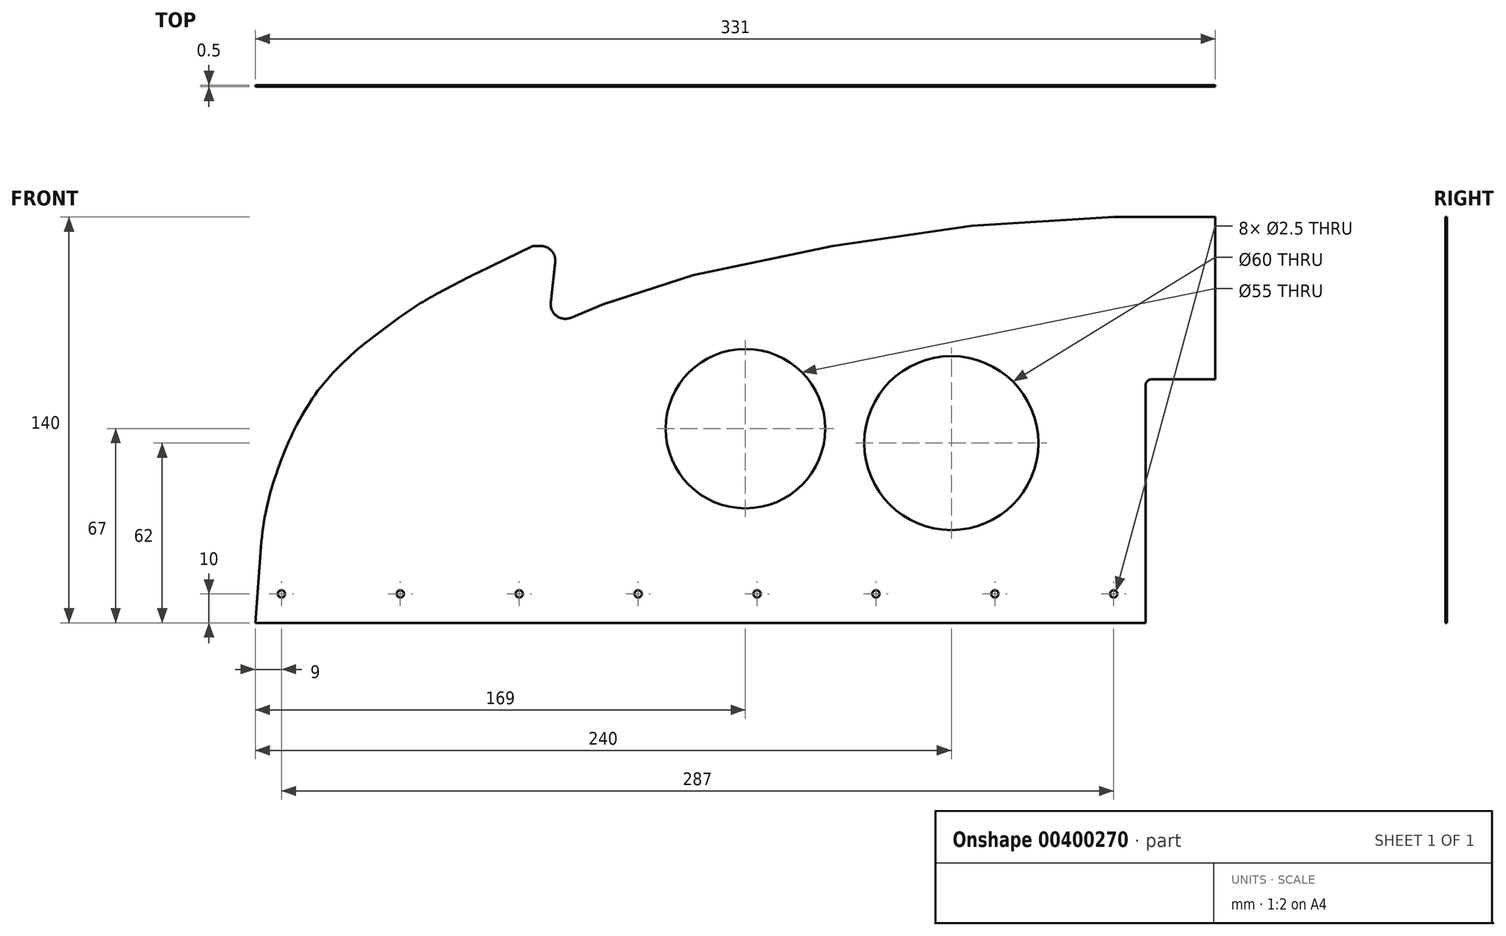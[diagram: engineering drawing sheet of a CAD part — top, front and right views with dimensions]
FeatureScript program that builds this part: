
annotation { "Feature Type Name" : "Feature", "Feature Type Description" : "" }
export const myFeature = defineFeature(function(context is Context, id is Id, definition is map)
    precondition{}
    {
        {
            var Q0;
            Q0=qCreatedBy(makeId("Front.planeOp"),FACE);
            var sketch = newSketch(context, id + "F0", { "sketchPlane" : qUnion([Q0])});
            skLineSegment(sketch, "E0", {"start": v(-24, 0) * mm, "end": v(-331, 0) * mm});
            skLineSegment(sketch, "E1", {"start": v(0, 84) * mm, "end": v(0, 140) * mm});
            skLineSegment(sketch, "E2", {"start": v(-331, 0) * mm, "end": v(-328, 40) * mm});
            skLineSegment(sketch, "E3", {"start": v(-328, 40) * mm, "end": v(-317, 70) * mm});
            skLineSegment(sketch, "E4", {"start": v(-317, 70) * mm, "end": v(-302, 90) * mm});
            skLineSegment(sketch, "E5", {"start": v(-302, 90) * mm, "end": v(-275, 110) * mm});
            skLineSegment(sketch, "E6", {"start": v(-275, 110) * mm, "end": v(-256, 120) * mm});
            skLineSegment(sketch, "E7", {"start": v(-256, 120) * mm, "end": v(-235.28, 130) * mm});
            skLineSegment(sketch, "E8", {"start": v(-235.28, 130) * mm, "end": v(-227, 130) * mm});
            skLineSegment(sketch, "E9", {"start": v(-227, 130) * mm, "end": v(-230, 102) * mm});
            skLineSegment(sketch, "E10", {"start": v(-132, 130) * mm, "end": v(-84, 137) * mm});
            skLineSegment(sketch, "E11", {"start": v(-84, 137) * mm, "end": v(-35, 140) * mm});
            skLineSegment(sketch, "E12", {"start": v(-35, 140) * mm, "end": v(0, 140) * mm});
            skLineSegment(sketch, "E13", {"start": v(-24, 0) * mm, "end": v(-24, 84) * mm});
            skLineSegment(sketch, "E14", {"start": v(-24, 84) * mm, "end": v(0, 84) * mm});
            skLineSegment(sketch, "E15", {"start": v(-132, 130) * mm, "end": v(-180, 120) * mm});
            skLineSegment(sketch, "E16", {"start": v(-180, 120) * mm, "end": v(-211, 110) * mm});
            skLineSegment(sketch, "E17", {"start": v(-211, 110) * mm, "end": v(-230, 102) * mm});
            skCircle(sketch, "E18", {"center": v(-91, 62) * mm, "radius": 30 * mm});
            skCircle(sketch, "E19", {"center": v(-162, 67) * mm, "radius": 27.5 * mm});
            skCircle(sketch, "E20", {"center": v(-35, 10) * mm, "radius": 1.25 * mm});
            skCircle(sketch, "E21.1.0.0", {"center": v(-76, 10) * mm, "radius": 1.25 * mm});
            skLineSegment(sketch, "E21.1.0.1", {"start": v(-65, 0) * mm, "end": v(-65, 84) * mm});
            skCircle(sketch, "E21.2.0.0", {"center": v(-117, 10) * mm, "radius": 1.25 * mm});
            skLineSegment(sketch, "E21.2.0.1", {"start": v(-106, 0) * mm, "end": v(-106, 84) * mm});
            skCircle(sketch, "E21.3.0.0", {"center": v(-158, 10) * mm, "radius": 1.25 * mm});
            skLineSegment(sketch, "E21.3.0.1", {"start": v(-147, 0) * mm, "end": v(-147, 84) * mm});
            skCircle(sketch, "E21.4.0.0", {"center": v(-199, 10) * mm, "radius": 1.25 * mm});
            skLineSegment(sketch, "E21.4.0.1", {"start": v(-188, 0) * mm, "end": v(-188, 84) * mm});
            skLineSegment(sketch, "E21.direction1", {"start": v(-35, 10) * mm, "end": v(-76, 10) * mm, "construction": true});
            skCircle(sketch, "E22.0.5.0", {"center": v(-240, 10) * mm, "radius": 1.25 * mm});
            skLineSegment(sketch, "E22.2.5.0", {"start": v(-229, 0) * mm, "end": v(-229, 84) * mm});
            skCircle(sketch, "E22.0.6.0", {"center": v(-281, 10) * mm, "radius": 1.25 * mm});
            skLineSegment(sketch, "E22.2.6.0", {"start": v(-270, 0) * mm, "end": v(-270, 84) * mm});
            skCircle(sketch, "E22.0.7.0", {"center": v(-322, 10) * mm, "radius": 1.25 * mm});
            skLineSegment(sketch, "E22.2.7.0", {"start": v(-311, 0) * mm, "end": v(-311, 84) * mm});
            skSolve(sketch);
        }
        {
            var Q0;
            Q0=makeQuery(id+"F0.imprint","IMPRINT",FACE,{"disambiguationData":[TD([[makeQuery(id+"F0.imprint","IMPRINT",EDGE,{"derivedFrom":sQuery(id+"F0.wireOp",EDGE,"E1")}),1.0]])]});
            var Q1;
            {var subQ1=sQuery(id+"F0.wireOp",EDGE,"E2");Q1=makeQuery(id+"F0.imprint","IMPRINT",FACE,{"disambiguationData":[TD([[makeQuery(id+"F0.imprint","IMPRINT",EDGE,{"derivedFrom":subQ1}),-1.0]])]});}
            var Q2;
            Q2=makeQuery(id+"F0.imprint","IMPRINT",FACE,{"disambiguationData":[TD([[makeQuery(id+"F0.imprint","IMPRINT",EDGE,{"derivedFrom":sQuery(id+"F0.wireOp",EDGE,"E21.3.0.0")}),-1.0]])]});
            var Q3;
            Q3=makeQuery(id+"F0.imprint","IMPRINT",FACE,{"disambiguationData":[TD([[makeQuery(id+"F0.imprint","IMPRINT",EDGE,{"derivedFrom":sQuery(id+"F0.wireOp",EDGE,"E21.1.0.0")}),-1.0]])]});
            extrude(context, id + "F1", {"entities" : qUnion([Q0, Q1, Q2, Q3]), "depth" : 0.5 * mm, "offsetDistance" : 25 * mm});
        }
        {
            var Q0;
            Q0=makeQuery(id+"F1.opExtrude","SWEPT_EDGE",EDGE,{"disambiguationData":[OSD([sQuery(id+"F0.wireOp",EDGE,"E9"),sQuery(id+"F0.wireOp",EDGE,"E17")])]});
            fillet(context, id + "F2", {"entities" : qUnion([Q0]), "tangentPropagation" : true, "radius" : 5 * mm, "defaultsChanged" : false, "vertexSettings" : [], "allowEdgeOverflow" : false});
        }
        {
            var Q0;
            Q0=makeQuery(id+"F1.opExtrude","SWEPT_EDGE",EDGE,{"disambiguationData":[OSD([sQuery(id+"F0.wireOp",EDGE,"E3"),sQuery(id+"F0.wireOp",EDGE,"E4")])]});
            var Q1;
            Q1=makeQuery(id+"F1.opExtrude","SWEPT_EDGE",EDGE,{"disambiguationData":[OSD([sQuery(id+"F0.wireOp",EDGE,"E6"),sQuery(id+"F0.wireOp",EDGE,"E7")])]});
            var Q2;
            Q2=makeQuery(id+"F1.opExtrude","SWEPT_EDGE",EDGE,{"disambiguationData":[OSD([sQuery(id+"F0.wireOp",EDGE,"E5"),sQuery(id+"F0.wireOp",EDGE,"E6")])]});
            var Q3;
            Q3=makeQuery(id+"F1.opExtrude","SWEPT_EDGE",EDGE,{"disambiguationData":[OSD([sQuery(id+"F0.wireOp",EDGE,"E4"),sQuery(id+"F0.wireOp",EDGE,"E5")])]});
            fillet(context, id + "F3", {"entities" : qUnion([Q0, Q1, Q2, Q3]), "tangentPropagation" : true, "radius" : 100 * mm, "defaultsChanged" : true, "vertexSettings" : [], "allowEdgeOverflow" : false});
        }
        {
            var Q0;
            Q0=makeQuery(id+"F1.opExtrude","SWEPT_EDGE",EDGE,{"disambiguationData":[OSD([sQuery(id+"F0.wireOp",EDGE,"E2"),sQuery(id+"F0.wireOp",EDGE,"E3")])]});
            fillet(context, id + "F4", {"entities" : qUnion([Q0]), "tangentPropagation" : true, "radius" : 100 * mm, "defaultsChanged" : true, "vertexSettings" : [], "allowEdgeOverflow" : false});
        }
        {
            var Q0;
            Q0=makeQuery(id+"F1.opExtrude","SWEPT_EDGE",EDGE,{"disambiguationData":[OSD([sQuery(id+"F0.wireOp",EDGE,"E8"),sQuery(id+"F0.wireOp",EDGE,"E9")])]});
            fillet(context, id + "F5", {"entities" : qUnion([Q0]), "tangentPropagation" : true, "radius" : 5 * mm, "defaultsChanged" : false, "vertexSettings" : [], "allowEdgeOverflow" : false});
        }
        {
            var Q0;
            Q0=makeQuery(id+"F1.opExtrude","SWEPT_EDGE",EDGE,{"disambiguationData":[OSD([sQuery(id+"F0.wireOp",EDGE,"E13"),sQuery(id+"F0.wireOp",EDGE,"E14")])]});
            fillet(context, id + "F6", {"entities" : qUnion([Q0]), "tangentPropagation" : true, "radius" : 2 * mm, "defaultsChanged" : true, "vertexSettings" : [], "allowEdgeOverflow" : false});
        }
    });
